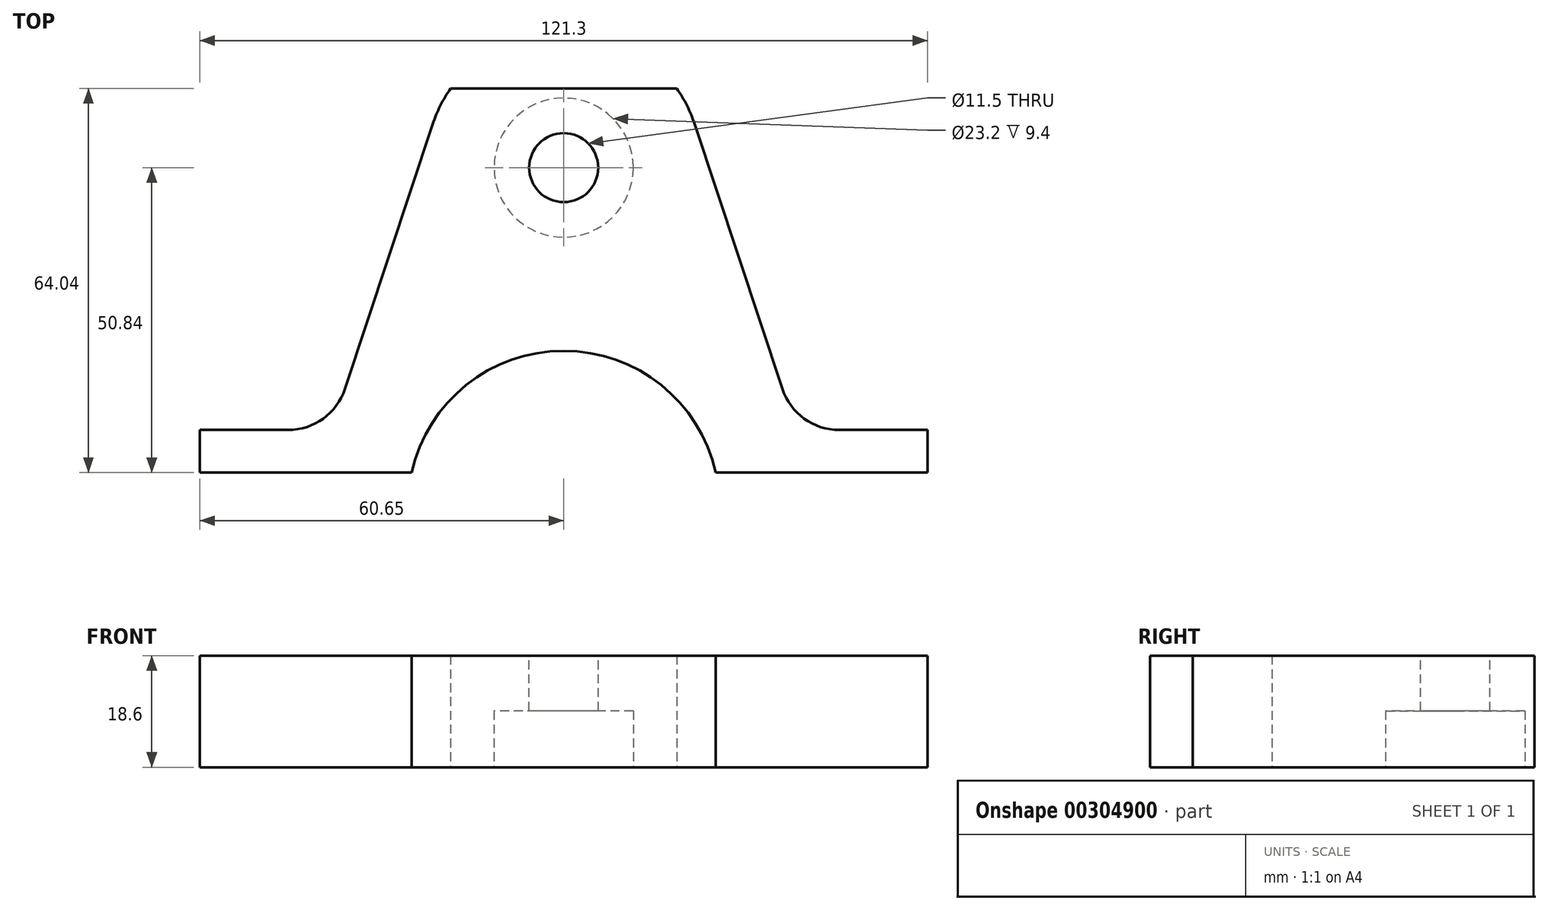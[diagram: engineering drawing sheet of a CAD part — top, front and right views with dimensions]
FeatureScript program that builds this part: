
annotation { "Feature Type Name" : "Feature", "Feature Type Description" : "" }
export const myFeature = defineFeature(function(context is Context, id is Id, definition is map)
    precondition{}
    {
        {
            var Q0;
            Q0=qCreatedBy(makeId("Top.planeOp"),FACE);
            var sketch = newSketch(context, id + "F0", { "sketchPlane" : qUnion([Q0])});
            skCircle(sketch, "E0", {"center": v(0, 0) * mm, "radius": 11.6 * mm});
            skArc(sketch, "E1", {"start": v(21.83, 7.23) * mm, "mid": v(0, 23) * mm, "end": v(-21.83, 7.23) * mm});
            skLineSegment(sketch, "E2", {"start": v(-21.83, 7.23) * mm, "end": v(-36.45, -36.88) * mm});
            skLineSegment(sketch, "E3.MirrorCS", {"start": v(21.83, 7.23) * mm, "end": v(36.45, -36.88) * mm});
            skLineSegment(sketch, "E4", {"start": v(-60.65, -43.73) * mm, "end": v(-60.65, -50.84) * mm});
            skLineSegment(sketch, "E5", {"start": v(-60.65, -50.84) * mm, "end": v(-25.37, -50.84) * mm});
            skLineSegment(sketch, "E6", {"start": v(60.65, -43.73) * mm, "end": v(45.94, -43.73) * mm});
            skPoint(sketch, "E7.orphan", {"position": v(-32.98, -26.4) * mm});
            skPoint(sketch, "E8.orphan", {"position": v(32.98, -26.4) * mm});
            skLineSegment(sketch, "E9", {"start": v(60.65, -43.73) * mm, "end": v(60.65, -50.84) * mm});
            skLineSegment(sketch, "E10.trimOffspring", {"start": v(-45.94, -43.73) * mm, "end": v(-60.65, -43.73) * mm});
            skPoint(sketch, "E11.visualSharp", {"position": v(-38.72, -43.73) * mm});
            skArc(sketch, "E11.filletArc", {"start": v(-45.94, -43.73) * mm, "mid": v(-40.09, -41.84) * mm, "end": v(-36.45, -36.88) * mm});
            skPoint(sketch, "E12.visualSharp", {"position": v(38.72, -43.73) * mm});
            skArc(sketch, "E12.filletArc", {"start": v(36.45, -36.88) * mm, "mid": v(40.09, -41.84) * mm, "end": v(45.94, -43.73) * mm});
            skArc(sketch, "E13", {"start": v(25.37, -50.84) * mm, "mid": v(0, -30.54) * mm, "end": v(-25.37, -50.84) * mm});
            skLineSegment(sketch, "E14.trimOffspring", {"start": v(25.37, -50.84) * mm, "end": v(60.65, -50.84) * mm});
            skSolve(sketch);
        }
        {
            var Q0;
            Q0 = qSketchRegion(id + "F0", true);
            extrude(context, id + "F1", {"entities" : qUnion([Q0]), "depth" : 25.4 * mm});
        }
        {
            var Q0;
            Q0=makeQuery(id+"F1.opExtrude","CAP_FACE",FACE,{"disambiguationData":[OSD([sQuery(id+"F0.wireOp",EDGE,"E0"),sQuery(id+"F0.wireOp",EDGE,"E1"),sQuery(id+"F0.wireOp",EDGE,"E2"),sQuery(id+"F0.wireOp",EDGE,"E3.MirrorCS"),sQuery(id+"F0.wireOp",EDGE,"E4"),sQuery(id+"F0.wireOp",EDGE,"E5"),sQuery(id+"F0.wireOp",EDGE,"E6"),sQuery(id+"F0.wireOp",EDGE,"E9"),sQuery(id+"F0.wireOp",EDGE,"E10.trimOffspring"),sQuery(id+"F0.wireOp",EDGE,"E11.filletArc"),sQuery(id+"F0.wireOp",EDGE,"E12.filletArc"),sQuery(id+"F0.wireOp",EDGE,"gBN4UQuN-eOoL-QXDF-XHs7-yzITmhE9s8hS"),sQuery(id+"F0.wireOp",EDGE,"E13"),sQuery(id+"F0.wireOp",EDGE,"E14.trimOffspring")])],"isStart":false});
            var sketch = newSketch(context, id + "F2", { "sketchPlane" : qUnion([Q0])});
            skCircle(sketch, "E15.0", {"center": v(0, 0) * mm, "radius": 11.6 * mm});
            skCircle(sketch, "E16", {"center": v(0, 0) * mm, "radius": 5.75 * mm});
            skSolve(sketch);
        }
        {
            var Q0;
            Q0 = qSketchRegion(id + "F2", true);
            extrude(context, id + "F3", {"entities" : qUnion([Q0]), "operationType" : NewBodyOperationType.ADD, "oppositeDirection" : true, "depth" : 16 * mm});
        }
        {
            var Q0;
            Q0=makeQuery(id+"F1.opExtrude","SWEPT_FACE",FACE,{"disambiguationData":[OSD([sQuery(id+"F0.wireOp",EDGE,"E6")])]});
            var sketch = newSketch(context, id + "F4", { "sketchPlane" : qUnion([Q0])});
            skCircle(sketch, "E17", {"center": v(-53.3, 12.7) * mm, "radius": 2.6 * mm});
            skLineSegment(sketch, "E18", {"start": v(-60.65, 12.7) * mm, "end": v(-53.3, 12.7) * mm, "construction": true});
            skCircle(sketch, "E19.MirrorC", {"center": v(53.3, 12.7) * mm, "radius": 2.6 * mm});
            skSolve(sketch);
        }
        {
            var Q0;
            Q0=makeQuery(id+"F4.imprint","IMPRINT",FACE,{"disambiguationData":[TD([[makeQuery(id+"F4.imprint","IMPRINT",EDGE,{"derivedFrom":sQuery(id+"F4.wireOp",EDGE,"E17")}),1.0]])]});
            var Q1;
            Q1=makeQuery(id+"F4.imprint","IMPRINT",FACE,{"disambiguationData":[TD([[makeQuery(id+"F4.imprint","IMPRINT",EDGE,{"derivedFrom":sQuery(id+"F4.wireOp",EDGE,"E19.MirrorC")}),-1.0]])]});
            extrude(context, id + "F5", {"entities" : qUnion([Q0, Q1]), "operationType" : NewBodyOperationType.REMOVE, "oppositeDirection" : true, "depth" : 25 * mm});
        }
        {
            var Q0;
            Q0=makeQuery(id+"F2.imprint","IMPRINT",FACE,{"disambiguationData":[TD([[makeQuery(id+"F2.imprint","IMPRINT",EDGE,{"derivedFrom":sQuery(id+"F2.wireOp",EDGE,"E15.0")}),-1.0]])]});
            extrude(context, id + "F6", {"entities" : qUnion([Q0]), "operationType" : NewBodyOperationType.ADD, "depth" : 13 * mm});
        }
        {
            var Q0;
            Q0=makeQuery(id+"F2.imprint","IMPRINT",FACE,{"disambiguationData":[TD([[makeQuery(id+"F2.imprint","IMPRINT",EDGE,{"derivedFrom":sQuery(id+"F2.wireOp",EDGE,"E15.0")}),1.0]])]});
            var Q1;
            Q1=makeQuery(id+"F6.opExtrude","CAP_FACE",FACE,{"disambiguationData":[OSD([sQuery(id+"F0.wireOp",EDGE,"E1"),sQuery(id+"F0.wireOp",EDGE,"E2"),sQuery(id+"F0.wireOp",EDGE,"E3.MirrorCS"),sQuery(id+"F0.wireOp",EDGE,"E4"),sQuery(id+"F0.wireOp",EDGE,"E5"),sQuery(id+"F0.wireOp",EDGE,"E6"),sQuery(id+"F0.wireOp",EDGE,"E9"),sQuery(id+"F0.wireOp",EDGE,"E10.trimOffspring"),sQuery(id+"F0.wireOp",EDGE,"E11.filletArc"),sQuery(id+"F0.wireOp",EDGE,"E12.filletArc"),sQuery(id+"F0.wireOp",EDGE,"E13"),sQuery(id+"F0.wireOp",EDGE,"E14.trimOffspring"),sQuery(id+"F2.wireOp",EDGE,"E15.0")])],"isStart":false});
            extrude(context, id + "F7", {"entities" : qUnion([Q0]), "operationType" : NewBodyOperationType.ADD, "endBound" : BoundingType.UP_TO_SURFACE, "endBoundEntityFace" : qUnion([Q1]), "depth" : 25 * mm});
        }
        {
            var Q0;
            Q0=makeQuery(id+"F0.imprint","IMPRINT",FACE,{"disambiguationData":[TD([[makeQuery(id+"F0.imprint","IMPRINT",EDGE,{"derivedFrom":sQuery(id+"F0.wireOp",EDGE,"E0")}),-1.0]])]});
            extrude(context, id + "F8", {"entities" : qUnion([Q0]), "operationType" : NewBodyOperationType.ADD, "depth" : 25 * mm});
        }
        {
            var Q0;
            Q0=qCreatedBy(makeId("Front.planeOp"),FACE);
            var sketch = newSketch(context, id + "F9", { "sketchPlane" : qUnion([Q0])});
            skLineSegment(sketch, "E20.bottom", {"start": v(42.88, 102.86) * mm, "end": v(-58.6, 102.86) * mm});
            skLineSegment(sketch, "E20.top", {"start": v(42.88, -60.28) * mm, "end": v(-58.6, -60.28) * mm});
            skLineSegment(sketch, "E20.left", {"start": v(42.88, 102.86) * mm, "end": v(42.88, -60.28) * mm});
            skLineSegment(sketch, "E20.right", {"start": v(-58.6, 102.86) * mm, "end": v(-58.6, -60.28) * mm});
            skSolve(sketch);
        }
        {
            var Q0;
            Q0 = qSketchRegion(id + "F9", true);
            extrude(context, id + "F10", {"entities" : qUnion([Q0]), "operationType" : NewBodyOperationType.REMOVE, "oppositeDirection" : true, "depth" : 28.8 * mm, "hasSecondDirection" : true, "secondDirectionOppositeDirection" : true, "secondDirectionDepth" : 13.2 * mm});
        }
        {
            var Q0;
            {var subQ0=sQuery(id+"F2.wireOp",EDGE,"E15.0");var subQ1=sQuery(id+"F0.wireOp",EDGE,"E14.trimOffspring");var subQ2=sQuery(id+"F0.wireOp",EDGE,"E13");var subQ3=sQuery(id+"F0.wireOp",EDGE,"E12.filletArc");var subQ4=sQuery(id+"F0.wireOp",EDGE,"E11.filletArc");var subQ5=sQuery(id+"F0.wireOp",EDGE,"E10.trimOffspring");var subQ6=sQuery(id+"F0.wireOp",EDGE,"E9");var subQ7=sQuery(id+"F0.wireOp",EDGE,"E6");var subQ8=sQuery(id+"F0.wireOp",EDGE,"E5");var subQ9=sQuery(id+"F0.wireOp",EDGE,"E4");var subQ10=sQuery(id+"F0.wireOp",EDGE,"E3.MirrorCS");var subQ11=sQuery(id+"F0.wireOp",EDGE,"E2");var subQ12=sQuery(id+"F0.wireOp",EDGE,"E1");Q0=makeQuery(id+"F7.boolean.opBoolean","MERGE",FACE,{"derivedFrom":[makeQuery(id+"F6.opExtrude","CAP_FACE",FACE,{"disambiguationData":[OSD([subQ12,subQ11,subQ10,subQ9,subQ8,subQ7,subQ6,subQ5,subQ4,subQ3,subQ2,subQ1,subQ0])],"isStart":false}),makeQuery(id+"F7.opExtrude","CAP_FACE",FACE,{"disambiguationData":[OSD([subQ12,subQ11,subQ10,subQ9,subQ8,subQ7,subQ6,subQ5,subQ4,subQ3,subQ2,subQ1,subQ0])],"isStart":false})]});}
            extrude(context, id + "F11", {"entities" : qUnion([Q0]), "operationType" : NewBodyOperationType.REMOVE, "oppositeDirection" : true, "depth" : 19.8 * mm});
        }
    });
